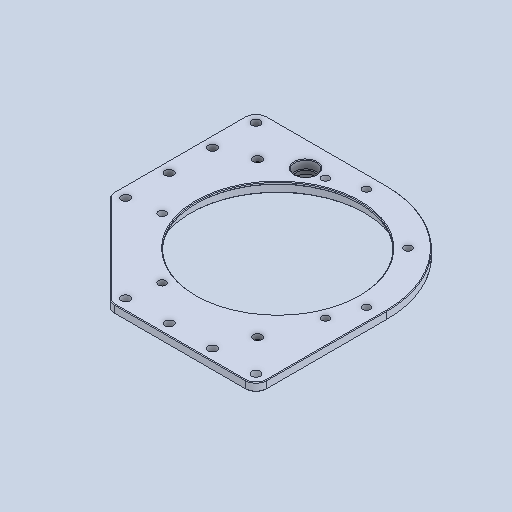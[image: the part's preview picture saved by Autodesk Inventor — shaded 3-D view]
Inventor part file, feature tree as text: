
AUTODESK INVENTOR PART (.ipt)
format: ipt  version: 2024.2 (Build 282272000, 272)  size: 248,320 bytes
history: native  units: in
note: dims shown in document units (in); Inventor stores cm internally (conversion verified against a paired STEP export)
features: chamfer x1
ambient origin geometry x8: Origin, YZ Plane, XZ Plane, XY Plane, X Axis, Y Axis, Z Axis, Center Point
bodies: Solid1 (feature_tree)
feature tree (1):
  chamfer  "Chamfer3"  [1 undecoded]
note: 1 required parameter value undecoded (feature->parameter linkage not recoverable at this tier; creation-order binding heuristic only, values carry confidence <= 0.55)
